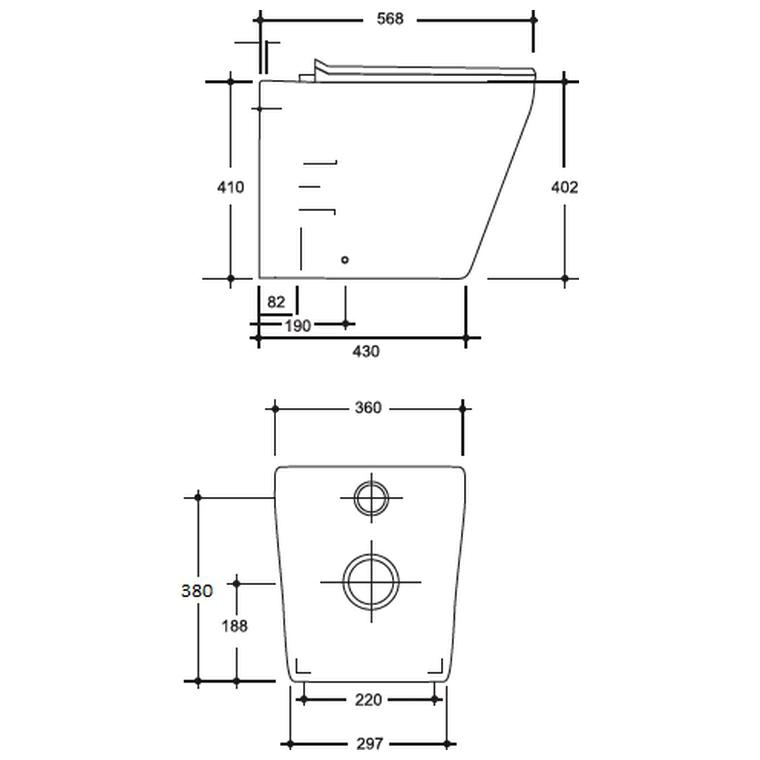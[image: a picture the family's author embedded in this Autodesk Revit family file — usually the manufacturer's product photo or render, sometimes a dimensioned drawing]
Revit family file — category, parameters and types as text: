
# Revit family: LIXIL - 772669WH - VAAL ENTICE RIMLESS CLOSE COUPLE SUITE
name_source: partatom
category: Plumbing Fixtures
units: mm (PartAtom-declared; Revit-internal decimal feet)

## family parameters
Always vertical = Yes
Cut with Voids When Loaded = No
Enable Cutting in Views = No
Maintain Annotation Orientation = No
OmniClass Number = 23.45.00.00
OmniClass Title = Sanitary, Laundry, and Cleaning Equipment
Part Type = Normal
Room Calculation Point = No
Round Connector Dimension = Use Diameter
Shared = Yes
Work Plane-Based = No

## types (1)
- 772669WH
    Default Elevation = 0 mm  [stored 0 ft]
    Description = Vaal wc to detail and spec. See sanware schedule. Available from Lixil.
    Hosted on lixil.co.za = https://www.lixil.co.za
    M _ CISTERN = M _ LIXIL - VAAL - PORCELAIN - WHITE 01
    M _ WC = M _ LIXIL - VAAL - PORCELAIN - WHITE 01
    M _ WC LID AND SEAT = M _ LIXIL - VAAL - PLASTIC - WHITE 01
    M _ WC SEAT SS FITTINGS = M _ LIXIL - STAINLESS STEEL 01
    M _ WC SEAT SUPPORT = M _ LIXIL - VAAL - PLASTIC - WHITE 01
    Product Specification = Supplier: Lixil.
Product description: Vaal Entice rimless cc suite, close coupled 90deg outlet rimless wash down pan and matching 6 litre top dual flush cistern, including soft close seat.
Product Code: CENT21SU-2CO0374.
SKU Code	: 772669WH.
Barcode: 6005826061178.
Brand: Vaal.
Range: Entice.
Category: Toilets.
Sub-Category: Close-Coupled Suites.
Material: Vitreous China.
Colour: White.
Package Height: 640 mm
Package Width: 450 mm
Package Length: 750 mm
Package Volume: 216000000 mm³
Package Weight: 54.85 kg

Notes:
- Refer to manufacturer's and supplier's installation, maintenance and cleaning manual.
- Refer to manufacturer's and supplier's guarantees and warrantees document.

note: [stored X ft] marks values corroborated as IEEE doubles in the binary element streams (Revit-internal decimal feet)

## geometry (parser evidence)
native form markers: Sweep x31
no freeform markers — native parametric forms only
